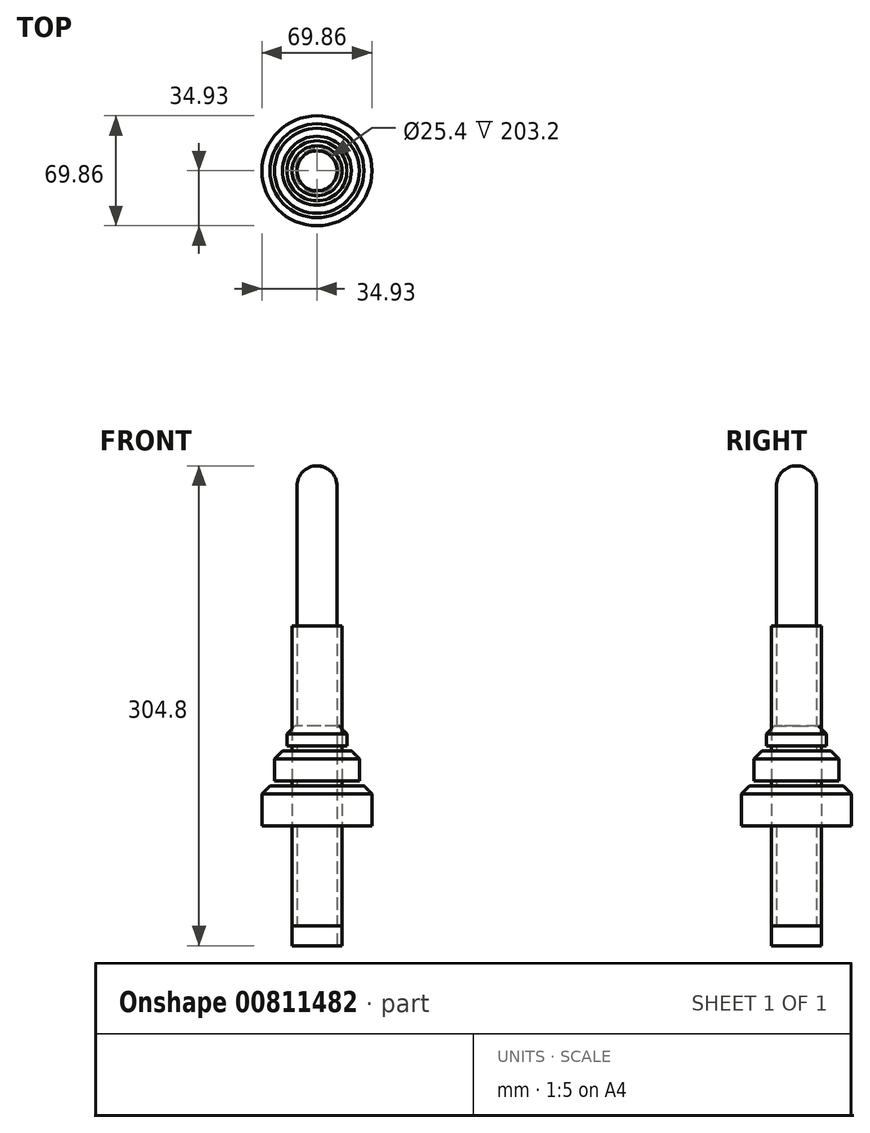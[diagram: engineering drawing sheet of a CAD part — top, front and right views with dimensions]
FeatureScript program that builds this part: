
annotation { "Feature Type Name" : "Feature", "Feature Type Description" : "" }
export const myFeature = defineFeature(function(context is Context, id is Id, definition is map)
    precondition{}
    {
        {
            var Q0;
            Q0=qCreatedBy(makeId("Top.planeOp"),FACE);
            var sketch = newSketch(context, id + "F0", { "sketchPlane" : qUnion([Q0])});
            skCircle(sketch, "E0", {"center": v(0, 0) * mm, "radius": 23.88 * mm});
            skCircle(sketch, "E1", {"center": v(0, 0) * mm, "radius": 34.93 * mm});
            skCircle(sketch, "E2", {"center": v(0, 0) * mm, "radius": 15.88 * mm});
            skCircle(sketch, "E3", {"center": v(0, 0) * mm, "radius": 19.05 * mm});
            skCircle(sketch, "E4", {"center": v(0, 0) * mm, "radius": 26.99 * mm});
            skCircle(sketch, "E5", {"center": v(0, 0) * mm, "radius": 12.7 * mm});
            skSolve(sketch);
        }
        {
            var Q0;
            Q0=makeQuery(id+"F0.imprint","IMPRINT",FACE,{"disambiguationData":[TD([[makeQuery(id+"F0.imprint","IMPRINT",EDGE,{"derivedFrom":sQuery(id+"F0.wireOp",EDGE,"E5")}),1.0]])]});
            var Q1;
            Q1=sQuery(id+"F0.wireOp",EDGE,"E5");
            extrude(context, id + "F1", {"entities" : qUnion([Q0]), "surfaceEntities" : qUnion([Q1]), "depth" : 304.8 * mm, "offsetDistance" : 25.4 * mm});
        }
        {
            var Q0;
            Q0=qCreatedBy(makeId("Top.planeOp"),FACE);
            cPlane(context, id + "F2", {"entities" : qUnion([Q0]), "cplaneType" : CPlaneType.OFFSET, "offset" : 76.2 * mm, "width" : 152.4 * mm, "height" : 152.4 * mm});
        }
        {
            var Q0;
            Q0=qCreatedBy(makeId("Top.planeOp"),FACE);
            cPlane(context, id + "F3", {"entities" : qUnion([Q0]), "cplaneType" : CPlaneType.OFFSET, "offset" : 104.77 * mm, "width" : 152.4 * mm, "height" : 152.4 * mm});
        }
        {
            var Q0;
            Q0=qCreatedBy(makeId("Top.planeOp"),FACE);
            cPlane(context, id + "F4", {"entities" : qUnion([Q0]), "cplaneType" : CPlaneType.OFFSET, "offset" : 127 * mm, "width" : 152.4 * mm, "height" : 152.4 * mm});
        }
        {
            var Q0;
            Q0=qCreatedBy(id+"F2.planeOp",FACE);
            var sketch = newSketch(context, id + "F5", { "sketchPlane" : qUnion([Q0])});
            skCircle(sketch, "E6.0", {"center": v(0, 0) * mm, "radius": 34.93 * mm});
            skSolve(sketch);
        }
        {
            var Q0;
            Q0=qCreatedBy(id+"F3.planeOp",FACE);
            var sketch = newSketch(context, id + "F6", { "sketchPlane" : qUnion([Q0])});
            skCircle(sketch, "E7.0", {"center": v(0, 0) * mm, "radius": 26.99 * mm});
            skSolve(sketch);
        }
        {
            var Q0;
            Q0=qCreatedBy(id+"F4.planeOp",FACE);
            var sketch = newSketch(context, id + "F7", { "sketchPlane" : qUnion([Q0])});
            skCircle(sketch, "E8.0", {"center": v(0, 0) * mm, "radius": 19.05 * mm});
            skSolve(sketch);
        }
        {
            var Q0;
            Q0=makeQuery(id+"F5.imprint","IMPRINT",FACE,{"disambiguationData":[TD([[makeQuery(id+"F5.imprint","IMPRINT",EDGE,{"derivedFrom":sQuery(id+"F5.wireOp",EDGE,"E6.0")}),1.0]])]});
            extrude(context, id + "F8", {"entities" : qUnion([Q0]), "operationType" : NewBodyOperationType.ADD, "depth" : 25.4 * mm, "offsetDistance" : 25.4 * mm});
        }
        {
            var Q0;
            Q0=makeQuery(id+"F6.imprint","IMPRINT",FACE,{"disambiguationData":[TD([[makeQuery(id+"F6.imprint","IMPRINT",EDGE,{"derivedFrom":sQuery(id+"F6.wireOp",EDGE,"E7.0")}),1.0]])]});
            var Q1;
            Q1=sQuery(id+"F6.wireOp",EDGE,"E7.0");
            extrude(context, id + "F9", {"entities" : qUnion([Q0]), "operationType" : NewBodyOperationType.ADD, "surfaceEntities" : qUnion([Q1]), "depth" : 19.05 * mm, "offsetDistance" : 25.4 * mm});
        }
        {
            var Q0;
            Q0=makeQuery(id+"F7.imprint","IMPRINT",FACE,{"disambiguationData":[TD([[makeQuery(id+"F7.imprint","IMPRINT",EDGE,{"derivedFrom":sQuery(id+"F7.wireOp",EDGE,"E8.0")}),1.0]])]});
            var Q1;
            Q1=makeQuery(id+"F0.imprint","IMPRINT",FACE,{"disambiguationData":[TD([[makeQuery(id+"F0.imprint","IMPRINT",EDGE,{"derivedFrom":sQuery(id+"F0.wireOp",EDGE,"E2")}),1.0]])]});
            var Q2;
            Q2=sQuery(id+"F7.wireOp",EDGE,"E8.0");
            extrude(context, id + "F10", {"entities" : qUnion([Q0, Q1]), "operationType" : NewBodyOperationType.ADD, "surfaceEntities" : qUnion([Q2]), "depth" : 12.7 * mm, "offsetDistance" : 25.4 * mm});
        }
        {
            var Q0;
            Q0=makeQuery(id+"F1.opExtrude","CAP_EDGE",EDGE,{"disambiguationData":[OSD([sQuery(id+"F0.wireOp",EDGE,"E5")])],"isStart":false});
            fillet(context, id + "F11", {"entities" : qUnion([Q0]), "radius" : 12.7 * mm, "tangentPropagation" : true, "allowEdgeOverflow" : false});
        }
        {
            var Q0;
            Q0=makeQuery(id+"F10.opExtrude","CAP_EDGE",EDGE,{"disambiguationData":[OSD([sQuery(id+"F7.wireOp",EDGE,"E8.0")])],"isStart":false});
            var Q1;
            Q1=makeQuery(id+"F9.opExtrude","CAP_EDGE",EDGE,{"disambiguationData":[OSD([sQuery(id+"F6.wireOp",EDGE,"E7.0")])],"isStart":false});
            var Q2;
            Q2=makeQuery(id+"F8.opExtrude","CAP_EDGE",EDGE,{"disambiguationData":[OSD([sQuery(id+"F5.wireOp",EDGE,"E6.0")])],"isStart":false});
            chamfer(context, id + "F12", {"entities" : qUnion([Q0, Q1, Q2]), "width" : 5.08 * mm, "tangentPropagation" : true});
        }
        {
            var Q0;
            Q0=makeQuery(id+"F0.imprint","IMPRINT",FACE,{"disambiguationData":[TD([[makeQuery(id+"F0.imprint","IMPRINT",EDGE,{"derivedFrom":sQuery(id+"F0.wireOp",EDGE,"E2")}),1.0]])]});
            var Q1;
            Q1=sQuery(id+"F0.wireOp",EDGE,"E2");
            extrude(context, id + "F13", {"entities" : qUnion([Q0]), "surfaceEntities" : qUnion([Q1]), "depth" : 203.2 * mm, "offsetDistance" : 25.4 * mm});
        }
    });
